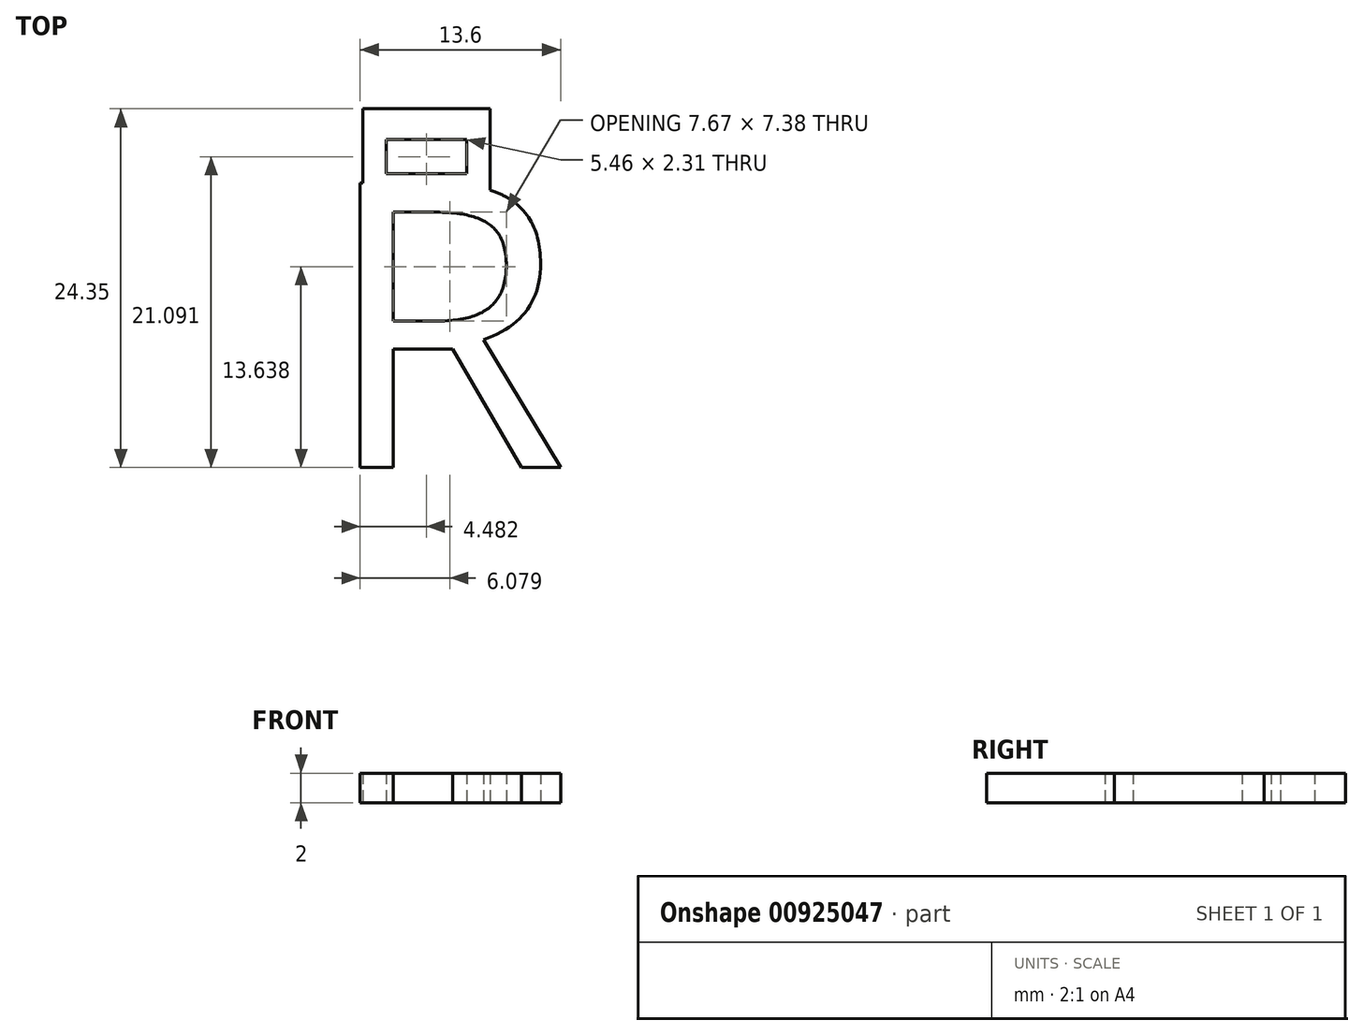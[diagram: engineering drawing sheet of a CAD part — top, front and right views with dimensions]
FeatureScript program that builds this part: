
annotation { "Feature Type Name" : "Feature", "Feature Type Description" : "" }
export const myFeature = defineFeature(function(context is Context, id is Id, definition is map)
    precondition{}
    {
        {
            var Q0;
            Q0=qCreatedBy(makeId("Top.planeOp"),FACE);
            var sketch = newSketch(context, id + "F0", { "sketchPlane" : qUnion([Q0])});
            skText(sketch, "E0", { "text": "R\n", "fontName": "OpenSans-Regular.ttf"});
            skLineSegment(sketch, "E1.bottom", {"start": v(2.81, -1.62) * mm, "end": v(11.45, -1.62) * mm});
            skLineSegment(sketch, "E1.top", {"start": v(2.81, 4.89) * mm, "end": v(11.45, 4.89) * mm});
            skLineSegment(sketch, "E1.left", {"start": v(2.81, -1.62) * mm, "end": v(2.81, 4.89) * mm});
            skLineSegment(sketch, "E1.right", {"start": v(11.45, -1.62) * mm, "end": v(11.45, 4.89) * mm});
            skLineSegment(sketch, "E2", {"start": v(7.13, 4.89) * mm, "end": v(7.13, -1.62) * mm});
            skLineSegment(sketch, "E3.bottom", {"start": v(9.86, 0.48) * mm, "end": v(4.4, 0.48) * mm});
            skLineSegment(sketch, "E3.top", {"start": v(9.86, 2.78) * mm, "end": v(4.4, 2.78) * mm});
            skLineSegment(sketch, "E3.left", {"start": v(9.86, 0.48) * mm, "end": v(9.86, 2.78) * mm});
            skLineSegment(sketch, "E3.right", {"start": v(4.4, 0.48) * mm, "end": v(4.4, 2.78) * mm});
            skPoint(sketch, "E3.middle", {"position": v(7.13, 1.63) * mm});
            const initialGuessF0  = {"E0": [0, -0.01946, 1, 0, 0.01946]};
            skSetInitialGuess(sketch, initialGuessF0);
            skSolve(sketch);
        }
        {
            var Q0;
            Q0 = qSketchRegion(id + "F0", true);
            extrude(context, id + "F1", {"entities" : qUnion([Q0]), "depth" : 2 * mm, "offsetDistance" : 25 * mm});
        }
    });
